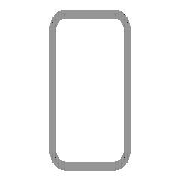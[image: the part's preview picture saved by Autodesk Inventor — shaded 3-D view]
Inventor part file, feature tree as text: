
AUTODESK INVENTOR PART (.ipt)
format: ipt  version: 2025 (Build 290162010, 162A)  size: 133,120 bytes
history: native  units: mm (DEFAULTED — no unit token found)
features: other x4, sketch x1, plane x1
ambient origin geometry x8: Origin, YZ Plane, XZ Plane, XY Plane, X Axis, Y Axis, Z Axis, Center Point
bodies: Solid1 (feature_tree), Body (feature_tree)
feature tree (6):
  parser-record x1  (decoder bookkeeping rows leaked as tree rows — omitted from the tree; the rows remain in map.json)
  other  "Driven Length"
  other  "Start Plane"
  other  "End Plane"
  sketch  "Sketch3"  dims[d3=850.0mm d4=0.0mm d7=6.0mm d9=40.0mm d11=60.0mm d12=3.0mm d13=-0.0mm d14=850.0mm d15=20.0mm d16=30.0mm d17=90.0deg d18=850.0mm]
  plane  "Work Plane3"
